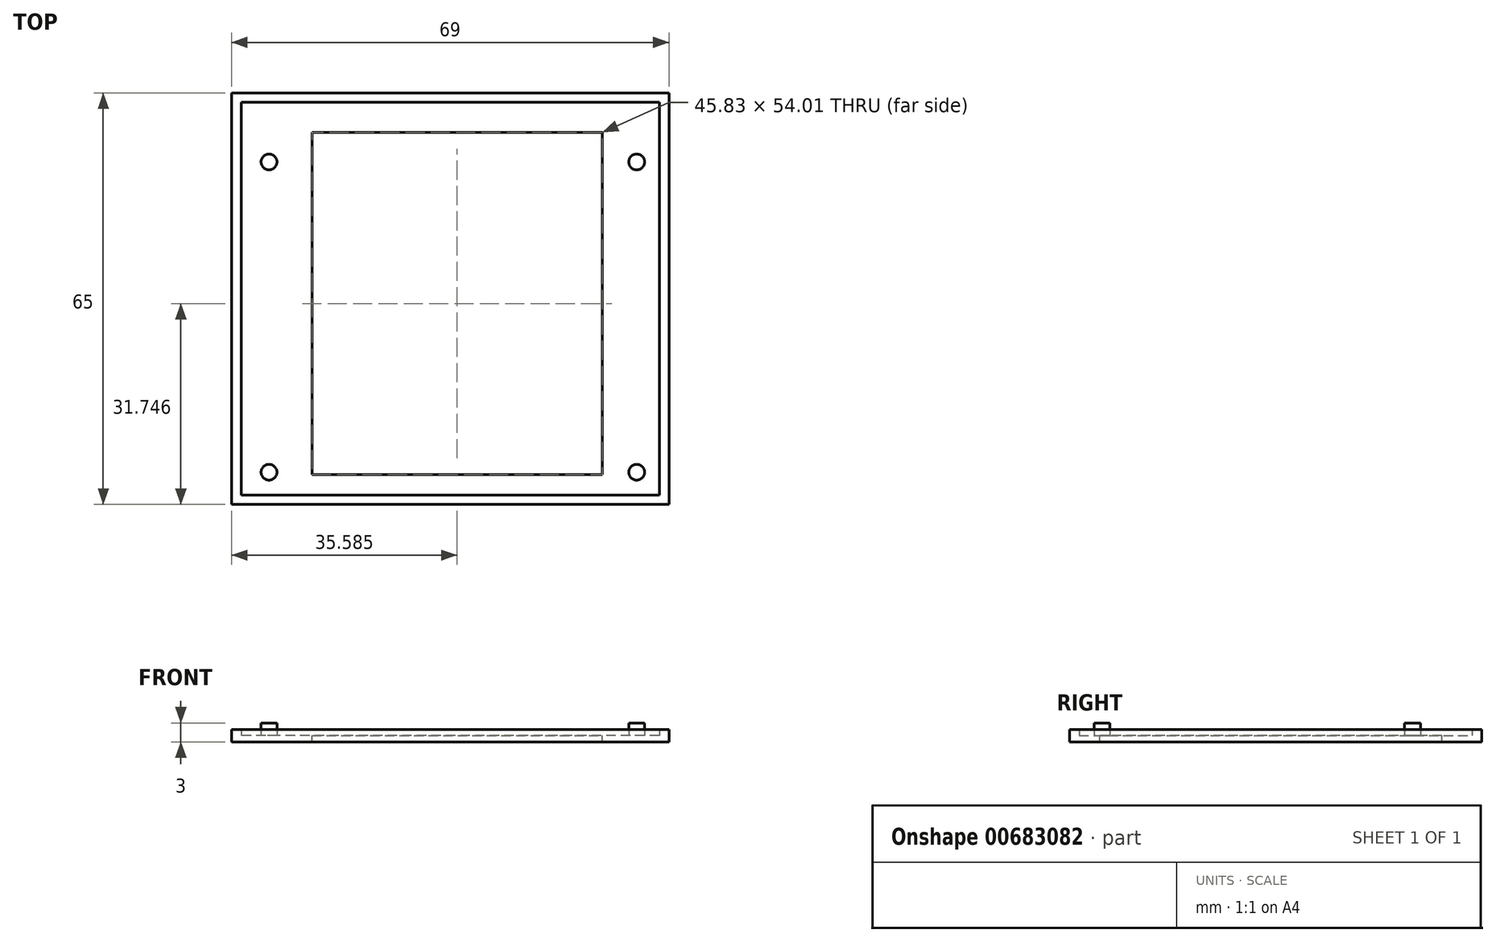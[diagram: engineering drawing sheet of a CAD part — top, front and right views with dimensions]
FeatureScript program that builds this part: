
annotation { "Feature Type Name" : "Feature", "Feature Type Description" : "" }
export const myFeature = defineFeature(function(context is Context, id is Id, definition is map)
    precondition{}
    {
        {
            var Q0;
            Q0=qCreatedBy(makeId("Top.planeOp"),FACE);
            var sketch = newSketch(context, id + "F0", { "sketchPlane" : qUnion([Q0])});
            skLineSegment(sketch, "E0.bottom", {"start": v(34.5, -32.5) * mm, "end": v(-34.5, -32.5) * mm});
            skLineSegment(sketch, "E0.top", {"start": v(34.5, 32.5) * mm, "end": v(-34.5, 32.5) * mm});
            skLineSegment(sketch, "E0.left", {"start": v(34.5, -32.5) * mm, "end": v(34.5, 32.5) * mm});
            skLineSegment(sketch, "E0.right", {"start": v(-34.5, -32.5) * mm, "end": v(-34.5, 32.5) * mm});
            skPoint(sketch, "E0.middle", {"position": v(0, 0) * mm});
            skSolve(sketch);
        }
        {
            var Q0;
            Q0=makeQuery(id+"F0.imprint","IMPRINT",FACE,{"disambiguationData":[TD([[makeQuery(id+"F0.imprint","IMPRINT",EDGE,{"derivedFrom":sQuery(id+"F0.wireOp",EDGE,"E0.bottom")}),-1.0]])]});
            extrude(context, id + "F1", {"entities" : qUnion([Q0]), "depth" : 1 * mm, "offsetDistance" : 25 * mm});
        }
        {
            var Q0;
            Q0=makeQuery(id+"F1.opExtrude","CAP_FACE",FACE,{"disambiguationData":[OSD([sQuery(id+"F0.wireOp",EDGE,"E0.bottom"),sQuery(id+"F0.wireOp",EDGE,"E0.top"),sQuery(id+"F0.wireOp",EDGE,"E0.left"),sQuery(id+"F0.wireOp",EDGE,"E0.right")])],"isStart":false});
            var sketch = newSketch(context, id + "F2", { "sketchPlane" : qUnion([Q0])});
            skLineSegment(sketch, "E1.bottom", {"start": v(-34.5, 32.5) * mm, "end": v(34.5, 32.5) * mm});
            skLineSegment(sketch, "E1.top", {"start": v(-33, 31) * mm, "end": v(33, 31) * mm});
            skLineSegment(sketch, "E1.left", {"start": v(-34.5, 32.5) * mm, "end": v(-34.5, 31) * mm});
            skLineSegment(sketch, "E1.right", {"start": v(34.5, 32.5) * mm, "end": v(34.5, 31) * mm});
            skLineSegment(sketch, "E2.bottom", {"start": v(34.5, 32.5) * mm, "end": v(33, 32.5) * mm});
            skLineSegment(sketch, "E2.top", {"start": v(34.5, -32.5) * mm, "end": v(33, -32.5) * mm});
            skLineSegment(sketch, "E2.left", {"start": v(34.5, 32.5) * mm, "end": v(34.5, -32.5) * mm});
            skLineSegment(sketch, "E2.right", {"start": v(33, 31) * mm, "end": v(33, -31) * mm});
            skLineSegment(sketch, "E3.bottom", {"start": v(34.5, -32.5) * mm, "end": v(-34.5, -32.5) * mm});
            skLineSegment(sketch, "E3.top", {"start": v(33, -31) * mm, "end": v(-33, -31) * mm});
            skLineSegment(sketch, "E3.left", {"start": v(34.5, -32.5) * mm, "end": v(34.5, -31) * mm});
            skLineSegment(sketch, "E3.right", {"start": v(-34.5, -32.5) * mm, "end": v(-34.5, -31) * mm});
            skLineSegment(sketch, "E4.bottom", {"start": v(-34.5, -32.5) * mm, "end": v(-33, -32.5) * mm});
            skLineSegment(sketch, "E4.top", {"start": v(-34.5, 32.5) * mm, "end": v(-33, 32.5) * mm});
            skLineSegment(sketch, "E4.left", {"start": v(-34.5, -32.5) * mm, "end": v(-34.5, 32.5) * mm});
            skLineSegment(sketch, "E4.right", {"start": v(-33, -31) * mm, "end": v(-33, 31) * mm});
            skSolve(sketch);
        }
        {
            var Q0;
            Q0=makeQuery(id+"F2.imprint","IMPRINT",FACE,{"disambiguationData":[TD([[makeQuery(id+"F2.imprint","IMPRINT",EDGE,{"derivedFrom":sQuery(id+"F2.wireOp",EDGE,"E1.bottom")}),1.0]])]});
            extrude(context, id + "F3", {"entities" : qUnion([Q0]), "operationType" : NewBodyOperationType.ADD, "depth" : 1 * mm, "offsetDistance" : 25 * mm});
        }
        {
            var Q0;
            Q0=makeQuery(id+"F1.opExtrude","CAP_FACE",FACE,{"disambiguationData":[OSD([sQuery(id+"F0.wireOp",EDGE,"E0.bottom"),sQuery(id+"F0.wireOp",EDGE,"E0.top"),sQuery(id+"F0.wireOp",EDGE,"E0.left"),sQuery(id+"F0.wireOp",EDGE,"E0.right")])],"isStart":false});
            var sketch = newSketch(context, id + "F4", { "sketchPlane" : qUnion([Q0])});
            skLineSegment(sketch, "E5", {"start": v(33, -31) * mm, "end": v(29.4, -31) * mm});
            skLineSegment(sketch, "E6", {"start": v(29.4, -31) * mm, "end": v(29.4, -27.4) * mm});
            skCircle(sketch, "E7", {"center": v(29.4, -27.4) * mm, "radius": 1.25 * mm});
            skLineSegment(sketch, "E8", {"start": v(29.4, -27.4) * mm, "end": v(29.4, 21.6) * mm});
            skCircle(sketch, "E9", {"center": v(29.4, 21.6) * mm, "radius": 1.25 * mm});
            skLineSegment(sketch, "E10", {"start": v(29.4, 21.6) * mm, "end": v(-28.6, 21.6) * mm});
            skCircle(sketch, "E11", {"center": v(-28.6, 21.6) * mm, "radius": 1.25 * mm});
            skLineSegment(sketch, "E12", {"start": v(29.4, -27.4) * mm, "end": v(-28.6, -27.4) * mm});
            skCircle(sketch, "E13", {"center": v(-28.6, -27.4) * mm, "radius": 1.25 * mm});
            skSolve(sketch);
        }
        {
            var Q0;
            Q0=makeQuery(id+"F4.imprint","IMPRINT",FACE,{"disambiguationData":[TD([[makeQuery(id+"F4.imprint","IMPRINT",EDGE,{"derivedFrom":sQuery(id+"F4.wireOp",EDGE,"E11")}),1.0]])]});
            var Q1;
            {var subQ0=sQuery(id+"F4.wireOp",EDGE,"E10");var subQ1=sQuery(id+"F4.wireOp",EDGE,"E8");var subQ2=makeQuery(id+"F4.imprint","INTERSECT",VERTEX,{"derivedFrom":[subQ1,subQ0]});Q1=makeQuery(id+"F4.imprint","IMPRINT",FACE,{"disambiguationData":[TD([[makeQuery(id+"F4.imprint","IMPRINT",EDGE,{"disambiguationData":[TD([[subQ2,1.0]])],"derivedFrom":subQ1}),-1.0]])]});}
            var Q2;
            {var subQ0=sQuery(id+"F4.wireOp",EDGE,"E10");var subQ1=sQuery(id+"F4.wireOp",EDGE,"E8");var subQ2=makeQuery(id+"F4.imprint","INTERSECT",VERTEX,{"derivedFrom":[subQ1,subQ0]});Q2=makeQuery(id+"F4.imprint","IMPRINT",FACE,{"disambiguationData":[TD([[makeQuery(id+"F4.imprint","IMPRINT",EDGE,{"disambiguationData":[TD([[subQ2,1.0]])],"derivedFrom":subQ1}),1.0]])]});}
            var Q3;
            {var subQ0=sQuery(id+"F4.wireOp",EDGE,"E12");var subQ1=sQuery(id+"F4.wireOp",EDGE,"E7");var subQ2=makeQuery(id+"F4.imprint","INTERSECT",VERTEX,{"derivedFrom":[subQ1,subQ0]});Q3=makeQuery(id+"F4.imprint","IMPRINT",FACE,{"disambiguationData":[TD([[makeQuery(id+"F4.imprint","IMPRINT",EDGE,{"disambiguationData":[TD([[subQ2,1.0]])],"derivedFrom":subQ1}),1.0]])]});}
            var Q4;
            {var subQ1=sQuery(id+"F4.wireOp",EDGE,"E6");var subQ3=sQuery(id+"F4.wireOp",EDGE,"E7");var subQ4=makeQuery(id+"F4.imprint","INTERSECT",VERTEX,{"derivedFrom":[subQ1,subQ3]});Q4=makeQuery(id+"F4.imprint","IMPRINT",FACE,{"disambiguationData":[TD([[makeQuery(id+"F4.imprint","IMPRINT",EDGE,{"disambiguationData":[TD([[subQ4,1.0]])],"derivedFrom":subQ3}),1.0]])]});}
            var Q5;
            {var subQ1=sQuery(id+"F4.wireOp",EDGE,"E6");var subQ3=sQuery(id+"F4.wireOp",EDGE,"E7");var subQ4=makeQuery(id+"F4.imprint","INTERSECT",VERTEX,{"derivedFrom":[subQ1,subQ3]});Q5=makeQuery(id+"F4.imprint","IMPRINT",FACE,{"disambiguationData":[TD([[makeQuery(id+"F4.imprint","IMPRINT",EDGE,{"disambiguationData":[TD([[subQ4,-1.0]])],"derivedFrom":subQ3}),1.0]])]});}
            var Q6;
            Q6=makeQuery(id+"F4.imprint","IMPRINT",FACE,{"disambiguationData":[TD([[makeQuery(id+"F4.imprint","IMPRINT",EDGE,{"derivedFrom":sQuery(id+"F4.wireOp",EDGE,"E13")}),1.0]])]});
            extrude(context, id + "F5", {"entities" : qUnion([Q0, Q1, Q2, Q3, Q4, Q5, Q6]), "operationType" : NewBodyOperationType.ADD, "depth" : 2 * mm, "offsetDistance" : 25 * mm});
        }
        {
            var Q0;
            Q0=makeQuery(id+"F1.opExtrude","CAP_FACE",FACE,{"disambiguationData":[OSD([sQuery(id+"F0.wireOp",EDGE,"E0.bottom"),sQuery(id+"F0.wireOp",EDGE,"E0.top"),sQuery(id+"F0.wireOp",EDGE,"E0.left"),sQuery(id+"F0.wireOp",EDGE,"E0.right")])],"isStart":false});
            var sketch = newSketch(context, id + "F6", { "sketchPlane" : qUnion([Q0])});
            skLineSegment(sketch, "E14.bottom", {"start": v(-21.83, 26.25) * mm, "end": v(24, 26.25) * mm});
            skLineSegment(sketch, "E14.top", {"start": v(-21.83, -27.76) * mm, "end": v(24, -27.76) * mm});
            skLineSegment(sketch, "E14.left", {"start": v(-21.83, 26.25) * mm, "end": v(-21.83, -27.76) * mm});
            skLineSegment(sketch, "E14.right", {"start": v(24, 26.25) * mm, "end": v(24, -27.76) * mm});
            skSolve(sketch);
        }
        {
            var Q0;
            Q0 = qSketchRegion(id + "F6", true);
            extrude(context, id + "F7", {"entities" : qUnion([Q0]), "operationType" : NewBodyOperationType.REMOVE, "oppositeDirection" : true, "depth" : 25 * mm, "offsetDistance" : 25 * mm});
        }
    });
